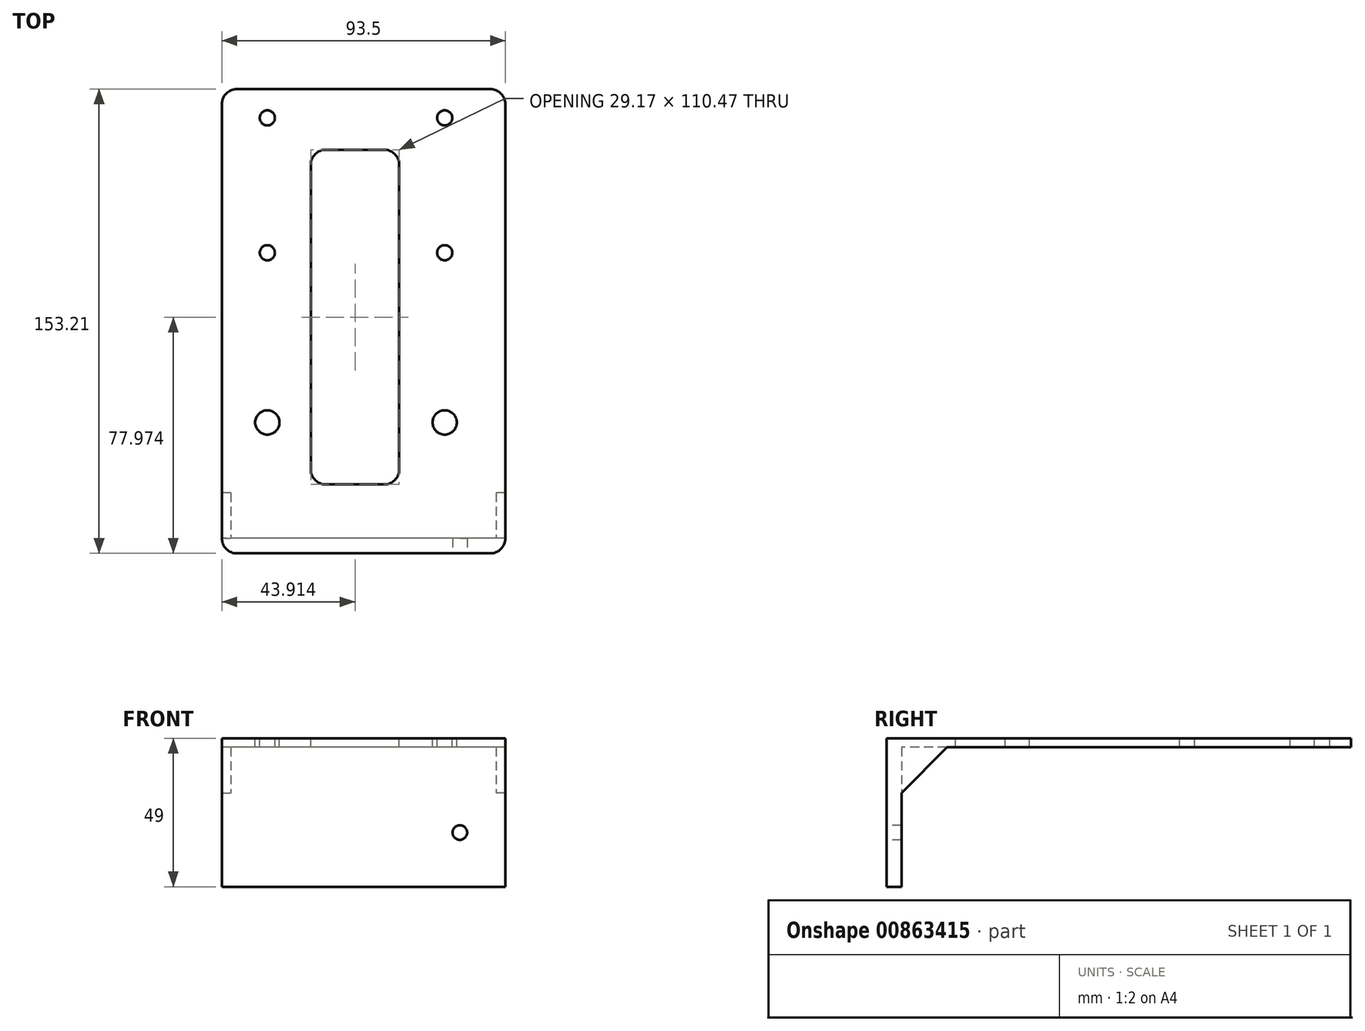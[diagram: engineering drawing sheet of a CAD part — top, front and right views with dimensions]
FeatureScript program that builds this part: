
annotation { "Feature Type Name" : "Feature", "Feature Type Description" : "" }
export const myFeature = defineFeature(function(context is Context, id is Id, definition is map)
    precondition{}
    {
        {
            var Q0;
            Q0=qCreatedBy(makeId("Top.planeOp"),FACE);
            var sketch = newSketch(context, id + "F0", { "sketchPlane" : qUnion([Q0])});
            skLineSegment(sketch, "E0.bottom", {"start": v(0, 0) * mm, "end": v(-93.5, 0) * mm});
            skLineSegment(sketch, "E0.top", {"start": v(0, 153.21) * mm, "end": v(-93.5, 153.21) * mm});
            skLineSegment(sketch, "E0.left", {"start": v(0, 0) * mm, "end": v(0, 153.2) * mm});
            skLineSegment(sketch, "E0.right", {"start": v(-93.5, 0) * mm, "end": v(-93.5, 153.21) * mm});
            skCircle(sketch, "E1", {"center": v(-20, 43.21) * mm, "radius": 4 * mm});
            skCircle(sketch, "E2", {"center": v(-78.5, 43.2) * mm, "radius": 4 * mm});
            skCircle(sketch, "E3", {"center": v(-78.5, 143.71) * mm, "radius": 2.5 * mm});
            skCircle(sketch, "E4", {"center": v(-78.5, 99.2) * mm, "radius": 2.5 * mm});
            skCircle(sketch, "E5", {"center": v(-20, 143.71) * mm, "radius": 2.5 * mm});
            skCircle(sketch, "E6", {"center": v(-20, 99.2) * mm, "radius": 2.5 * mm});
            skLineSegment(sketch, "E7.bottom", {"start": v(-35, 133.21) * mm, "end": v(-64.17, 133.21) * mm});
            skLineSegment(sketch, "E7.top", {"start": v(-35, 22.74) * mm, "end": v(-64.17, 22.74) * mm});
            skLineSegment(sketch, "E7.left", {"start": v(-35, 133.21) * mm, "end": v(-35, 22.74) * mm});
            skLineSegment(sketch, "E7.right", {"start": v(-64.17, 133.21) * mm, "end": v(-64.17, 22.74) * mm});
            skSolve(sketch);
        }
        {
            var Q0;
            Q0=makeQuery(id+"F0.imprint","IMPRINT",FACE,{"disambiguationData":[TD([[makeQuery(id+"F0.imprint","IMPRINT",EDGE,{"derivedFrom":sQuery(id+"F0.wireOp",EDGE,"E0.bottom")}),-1.0]])]});
            extrude(context, id + "F1", {"entities" : qUnion([Q0]), "oppositeDirection" : true, "depth" : 3 * mm, "offsetDistance" : 25 * mm});
        }
        {
            var Q0;
            Q0=makeQuery(id+"F1.opExtrude","CAP_FACE",FACE,{"disambiguationData":[OSD([sQuery(id+"F0.wireOp",EDGE,"E0.bottom"),sQuery(id+"F0.wireOp",EDGE,"E0.top"),sQuery(id+"F0.wireOp",EDGE,"E0.left"),sQuery(id+"F0.wireOp",EDGE,"E0.right"),sQuery(id+"F0.wireOp",EDGE,"E1"),sQuery(id+"F0.wireOp",EDGE,"E2"),sQuery(id+"F0.wireOp",EDGE,"E3"),sQuery(id+"F0.wireOp",EDGE,"E4"),sQuery(id+"F0.wireOp",EDGE,"E5"),sQuery(id+"F0.wireOp",EDGE,"E6"),sQuery(id+"F0.wireOp",EDGE,"E7.bottom"),sQuery(id+"F0.wireOp",EDGE,"E7.top"),sQuery(id+"F0.wireOp",EDGE,"E7.left"),sQuery(id+"F0.wireOp",EDGE,"E7.right")])],"isStart":false});
            var sketch = newSketch(context, id + "F2", { "sketchPlane" : qUnion([Q0])});
            skLineSegment(sketch, "E8.bottom", {"start": v(0, 0) * mm, "end": v(-93.5, 0) * mm});
            skLineSegment(sketch, "E8.top", {"start": v(0, -5) * mm, "end": v(-93.5, -5) * mm});
            skLineSegment(sketch, "E8.left", {"start": v(0, 0) * mm, "end": v(0, -5) * mm});
            skLineSegment(sketch, "E8.right", {"start": v(-93.5, 0) * mm, "end": v(-93.5, -5) * mm});
            skSolve(sketch);
        }
        {
            var Q0;
            Q0=makeQuery(id+"F2.imprint","IMPRINT",FACE,{"disambiguationData":[TD([[makeQuery(id+"F2.imprint","IMPRINT",EDGE,{"derivedFrom":sQuery(id+"F2.wireOp",EDGE,"E8.bottom")}),1.0]])]});
            extrude(context, id + "F3", {"entities" : qUnion([Q0]), "operationType" : NewBodyOperationType.ADD, "depth" : 46 * mm, "offsetDistance" : 25 * mm});
        }
        {
            var Q0;
            Q0=makeQuery(id+"F3.boolean.opBoolean","MERGE",FACE,{"derivedFrom":[makeQuery(id+"F1.opExtrude","SWEPT_FACE",FACE,{"disambiguationData":[OSD([sQuery(id+"F0.wireOp",EDGE,"E0.bottom")])]}),makeQuery(id+"F3.opExtrude","SWEPT_FACE",FACE,{"disambiguationData":[OSD([sQuery(id+"F2.wireOp",EDGE,"E8.bottom")])]})]});
            var sketch = newSketch(context, id + "F4", { "sketchPlane" : qUnion([Q0])});
            skCircle(sketch, "E9", {"center": v(-15, -31.12) * mm, "radius": 2.4 * mm});
            skSolve(sketch);
        }
        {
            var Q0;
            Q0=makeQuery(id+"F4.imprint","IMPRINT",FACE,{"disambiguationData":[TD([[makeQuery(id+"F4.imprint","IMPRINT",EDGE,{"derivedFrom":sQuery(id+"F4.wireOp",EDGE,"E9")}),1.0]])]});
            extrude(context, id + "F5", {"entities" : qUnion([Q0]), "operationType" : NewBodyOperationType.REMOVE, "endBound" : BoundingType.UP_TO_NEXT, "oppositeDirection" : true, "depth" : 25 * mm, "offsetDistance" : 25 * mm});
        }
        {
            var Q0;
            Q0=makeQuery(id+"F3.opExtrude","SWEPT_FACE",FACE,{"disambiguationData":[OSD([sQuery(id+"F2.wireOp",EDGE,"E8.top")])]});
            var sketch = newSketch(context, id + "F6", { "sketchPlane" : qUnion([Q0])});
            skLineSegment(sketch, "E10.bottom", {"start": v(0, -3) * mm, "end": v(3, -3) * mm});
            skLineSegment(sketch, "E10.top", {"start": v(0, -18) * mm, "end": v(3, -18) * mm});
            skLineSegment(sketch, "E10.left", {"start": v(0, -3) * mm, "end": v(0, -18) * mm});
            skLineSegment(sketch, "E10.right", {"start": v(3, -3) * mm, "end": v(3, -18) * mm});
            skLineSegment(sketch, "E11.bottom", {"start": v(93.5, -3) * mm, "end": v(90.5, -3) * mm});
            skLineSegment(sketch, "E11.top", {"start": v(93.5, -18) * mm, "end": v(90.5, -18) * mm});
            skLineSegment(sketch, "E11.left", {"start": v(93.5, -3) * mm, "end": v(93.5, -18) * mm});
            skLineSegment(sketch, "E11.right", {"start": v(90.5, -3) * mm, "end": v(90.5, -18) * mm});
            skSolve(sketch);
        }
        {
            var Q0;
            Q0=makeQuery(id+"F6.imprint","IMPRINT",FACE,{"disambiguationData":[TD([[makeQuery(id+"F6.imprint","IMPRINT",EDGE,{"derivedFrom":sQuery(id+"F6.wireOp",EDGE,"E10.bottom")}),-1.0]])]});
            var Q1;
            Q1=makeQuery(id+"F6.imprint","IMPRINT",FACE,{"disambiguationData":[TD([[makeQuery(id+"F6.imprint","IMPRINT",EDGE,{"derivedFrom":sQuery(id+"F6.wireOp",EDGE,"E11.bottom")}),-1.0]])]});
            extrude(context, id + "F7", {"entities" : qUnion([Q0, Q1]), "operationType" : NewBodyOperationType.ADD, "depth" : 15 * mm, "offsetDistance" : 25 * mm});
        }
        {
            var Q0;
            Q0=makeQuery(id+"F7.boolean.opBoolean","MERGE",FACE,{"derivedFrom":[makeQuery(id+"F3.boolean.opBoolean","MERGE",FACE,{"derivedFrom":[makeQuery(id+"F1.opExtrude","SWEPT_FACE",FACE,{"disambiguationData":[OSD([sQuery(id+"F0.wireOp",EDGE,"E0.right")])]}),makeQuery(id+"F3.opExtrude","SWEPT_FACE",FACE,{"disambiguationData":[OSD([sQuery(id+"F2.wireOp",EDGE,"E8.right")])]})]}),makeQuery(id+"F7.opExtrude","SWEPT_FACE",FACE,{"disambiguationData":[OSD([sQuery(id+"F6.wireOp",EDGE,"E11.left")])]})]});
            var sketch = newSketch(context, id + "F8", { "sketchPlane" : qUnion([Q0])});
            skLineSegment(sketch, "E12", {"start": v(-20, -3) * mm, "end": v(-5, -18) * mm});
            skSolve(sketch);
        }
        {
            var Q0;
            Q0=makeQuery(id+"F8.imprint","IMPRINT",FACE,{"disambiguationData":[TD([[makeQuery(id+"F8.imprint","IMPRINT",EDGE,{"derivedFrom":sQuery(id+"F8.wireOp",EDGE,"E12")}),-1.0]])]});
            extrude(context, id + "F9", {"entities" : qUnion([Q0]), "operationType" : NewBodyOperationType.REMOVE, "endBound" : BoundingType.THROUGH_ALL, "oppositeDirection" : true, "depth" : 25 * mm, "offsetDistance" : 25 * mm});
        }
        {
            var Q0;
            Q0=makeQuery(id+"F1.opExtrude","SWEPT_EDGE",EDGE,{"disambiguationData":[OSD([sQuery(id+"F0.wireOp",EDGE,"E0.top"),sQuery(id+"F0.wireOp",EDGE,"E0.left")])]});
            var Q1;
            Q1=makeQuery(id+"F1.opExtrude","SWEPT_EDGE",EDGE,{"disambiguationData":[OSD([sQuery(id+"F0.wireOp",EDGE,"E0.top"),sQuery(id+"F0.wireOp",EDGE,"E0.right")])]});
            var Q2;
            Q2=makeQuery(id+"F3.boolean.opBoolean","MERGE",EDGE,{"derivedFrom":[makeQuery(id+"F1.opExtrude","SWEPT_EDGE",EDGE,{"disambiguationData":[OSD([sQuery(id+"F0.wireOp",EDGE,"E0.bottom"),sQuery(id+"F0.wireOp",EDGE,"E0.left")])]}),makeQuery(id+"F3.opExtrude","SWEPT_EDGE",EDGE,{"disambiguationData":[OSD([sQuery(id+"F2.wireOp",EDGE,"E8.bottom"),sQuery(id+"F2.wireOp",EDGE,"E8.left")])]})]});
            var Q3;
            Q3=makeQuery(id+"F3.boolean.opBoolean","MERGE",EDGE,{"derivedFrom":[makeQuery(id+"F1.opExtrude","SWEPT_EDGE",EDGE,{"disambiguationData":[OSD([sQuery(id+"F0.wireOp",EDGE,"E0.bottom"),sQuery(id+"F0.wireOp",EDGE,"E0.right")])]}),makeQuery(id+"F3.opExtrude","SWEPT_EDGE",EDGE,{"disambiguationData":[OSD([sQuery(id+"F2.wireOp",EDGE,"E8.bottom"),sQuery(id+"F2.wireOp",EDGE,"E8.right")])]})]});
            var Q4;
            Q4=makeQuery(id+"F1.opExtrude","SWEPT_EDGE",EDGE,{"disambiguationData":[OSD([sQuery(id+"F0.wireOp",EDGE,"E7.bottom"),sQuery(id+"F0.wireOp",EDGE,"E7.right")])]});
            var Q5;
            Q5=makeQuery(id+"F1.opExtrude","SWEPT_EDGE",EDGE,{"disambiguationData":[OSD([sQuery(id+"F0.wireOp",EDGE,"E7.top"),sQuery(id+"F0.wireOp",EDGE,"E7.right")])]});
            var Q6;
            Q6=makeQuery(id+"F1.opExtrude","SWEPT_EDGE",EDGE,{"disambiguationData":[OSD([sQuery(id+"F0.wireOp",EDGE,"E7.top"),sQuery(id+"F0.wireOp",EDGE,"E7.left")])]});
            var Q7;
            Q7=makeQuery(id+"F1.opExtrude","SWEPT_EDGE",EDGE,{"disambiguationData":[OSD([sQuery(id+"F0.wireOp",EDGE,"E7.bottom"),sQuery(id+"F0.wireOp",EDGE,"E7.left")])]});
            fillet(context, id + "F10", {"entities" : qUnion([Q0, Q1, Q2, Q3, Q4, Q5, Q6, Q7]), "radius" : 5 * mm, "tangentPropagation" : true, "allowEdgeOverflow" : false});
        }
    });
